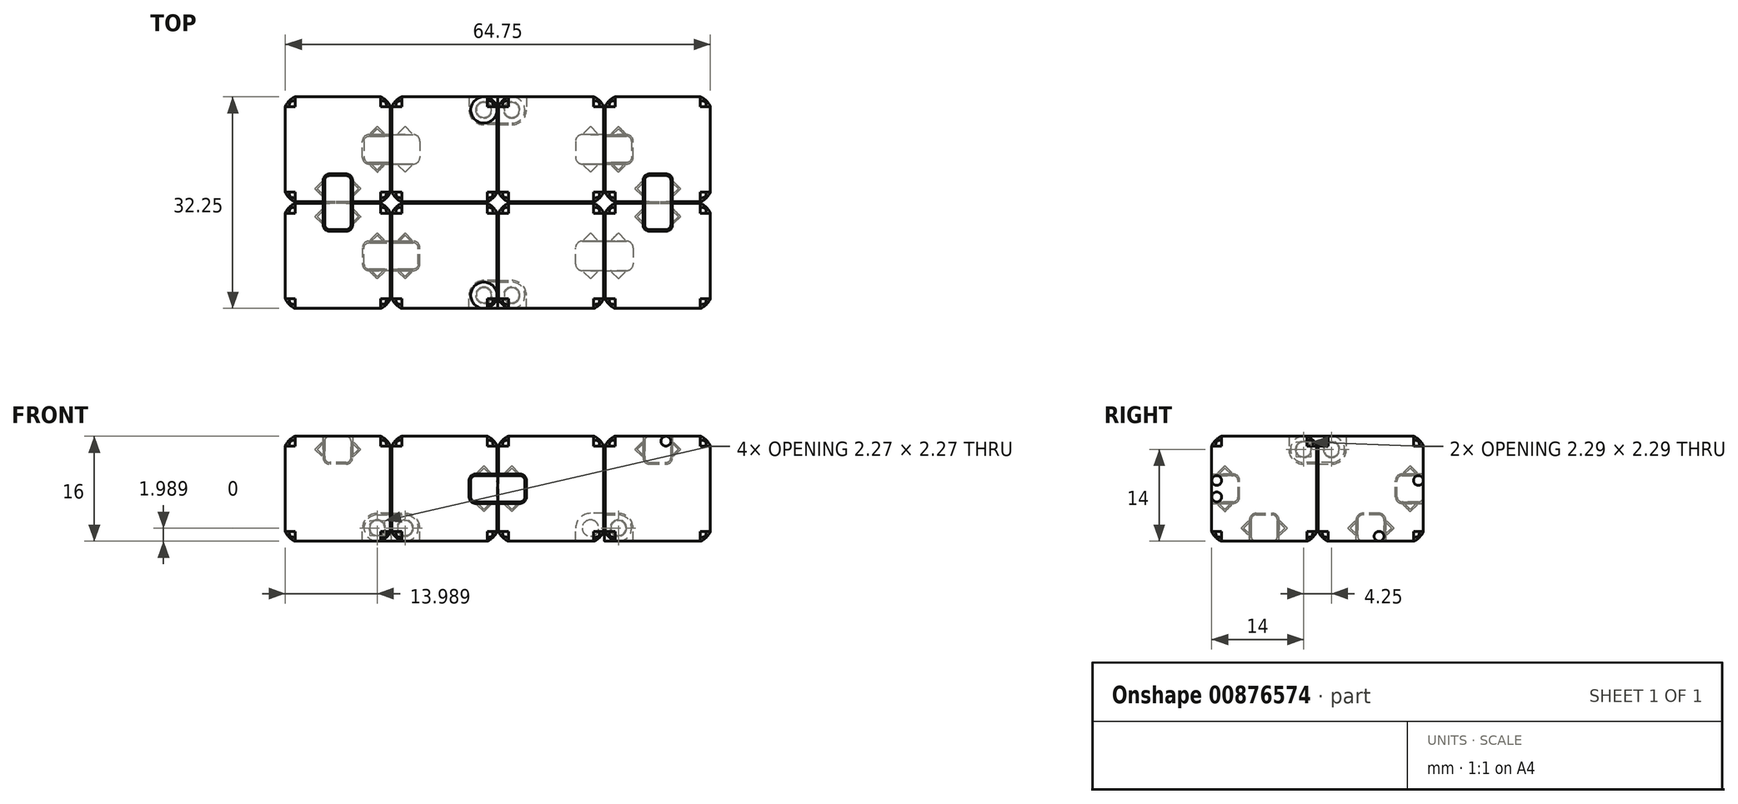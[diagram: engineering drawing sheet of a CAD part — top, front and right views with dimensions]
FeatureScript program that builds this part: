
annotation { "Feature Type Name" : "Feature", "Feature Type Description" : "" }
export const myFeature = defineFeature(function(context is Context, id is Id, definition is map)
    precondition{}
    {
        {
            assignVariable(context, id + "F0", {"name" : "cubeSize", "anyValue" : 16});
        }
        {
            assignVariable(context, id + "F1", {"name" : "hingeSize", "anyValue" : getVariable(context, 'cubeSize') / 4});
        }
        {
            assignVariable(context, id + "F2", {"name" : "hingeDiameter", "anyValue" : getVariable(context, 'hingeSize') / 2});
        }
        {
            assignVariable(context, id + "F3", {"name" : "minThickness", "anyValue" : 1});
        }
        {
            assignVariable(context, id + "F4", {"name" : "hingeGap", "anyValue" : .25});
        }
        {
            var Q0;
            Q0=qCreatedBy(makeId("Top.planeOp"),FACE);
            var sketch = newSketch(context, id + "F5", { "sketchPlane" : qUnion([Q0])});
            skLineSegment(sketch, "E0.bottom", {"start": v(8, -8) * mm, "end": v(-8, -8) * mm});
            skLineSegment(sketch, "E0.top", {"start": v(8, 8) * mm, "end": v(-8, 8) * mm});
            skLineSegment(sketch, "E0.left", {"start": v(8, -8) * mm, "end": v(8, 8) * mm});
            skLineSegment(sketch, "E0.right", {"start": v(-8, -8) * mm, "end": v(-8, 8) * mm});
            skPoint(sketch, "E0.middle", {"position": v(0, 0) * mm});
            skSolve(sketch);
        }
        {
            var Q0;
            Q0=qSketchRegion(id+"F5",true);
            extrude(context, id + "F6", {"entities" : qUnion([Q0]), "depth" : (getVariable(context, 'cubeSize')) * mm, "offsetDistance" : 25 * mm});
        }
        {
            var Q0;
            Q0=qCreatedBy(makeId("Front.planeOp"),FACE);
            var sketch = newSketch(context, id + "F7", { "sketchPlane" : qUnion([Q0])});
            skCircle(sketch, "E1", {"center": v(6, 2) * mm, "radius": 1 * mm});
            skLineSegment(sketch, "E2", {"start": v(6, 2) * mm, "end": v(7, 2) * mm, "construction": true});
            skLineSegment(sketch, "E3", {"start": v(7, 2) * mm, "end": v(8, 2) * mm, "construction": true});
            skLineSegment(sketch, "E4", {"start": v(6, 0) * mm, "end": v(6, 1) * mm, "construction": true});
            skLineSegment(sketch, "E5", {"start": v(6, 1) * mm, "end": v(6, 2) * mm, "construction": true});
            skLineSegment(sketch, "E6", {"start": v(8, 0) * mm, "end": v(3.75, 0) * mm});
            skLineSegment(sketch, "E7", {"start": v(3.75, 0) * mm, "end": v(3.75, 2) * mm});
            skLineSegment(sketch, "E8", {"start": v(8, 0) * mm, "end": v(8, 4.25) * mm});
            skLineSegment(sketch, "E9", {"start": v(8, 4.25) * mm, "end": v(6, 4.25) * mm});
            skArc(sketch, "E10", {"start": v(6, 4.25) * mm, "mid": v(4.4, 3.6) * mm, "end": v(3.75, 2) * mm});
            skSolve(sketch);
        }
        {
            var Q0;
            Q0=makeQuery(id+"F7.imprint","IMPRINT",FACE,{"disambiguationData":[TD([[makeQuery(id+"F7.imprint","IMPRINT",EDGE,{"derivedFrom":sQuery(id+"F7.wireOp",EDGE,"E1")}),-1.0]])]});
            var Q1;
            Q1=makeQuery(id+"F7.imprint","IMPRINT",FACE,{"disambiguationData":[TD([[makeQuery(id+"F7.imprint","IMPRINT",EDGE,{"derivedFrom":sQuery(id+"F7.wireOp",EDGE,"E1")}),1.0]])]});
            extrude(context, id + "F8", {"entities" : qUnion([Q0, Q1]), "operationType" : NewBodyOperationType.REMOVE, "endBound" : BoundingType.SYMMETRIC, "oppositeDirection" : true, "depth" : (getVariable(context, 'hingeSize') + getVariable(context, 'hingeGap') * 2) * mm, "offsetDistance" : 25 * mm});
        }
        {
            var Q0;
            Q0=makeQuery(id+"F6.opExtrude","CAP_VERTEX",VERTEX,{"disambiguationData":[OSD([sQuery(id+"F5.wireOp",EDGE,"E0.bottom"),sQuery(id+"F5.wireOp",EDGE,"E0.right")])],"isStart":false});
            var Q1;
            Q1=makeQuery(id+"F6.opExtrude","CAP_VERTEX",VERTEX,{"disambiguationData":[OSD([sQuery(id+"F5.wireOp",EDGE,"E0.bottom"),sQuery(id+"F5.wireOp",EDGE,"E0.left")])],"isStart":true});
            var Q2;
            Q2=makeQuery(id+"F6.opExtrude","CAP_VERTEX",VERTEX,{"disambiguationData":[OSD([sQuery(id+"F5.wireOp",EDGE,"E0.top"),sQuery(id+"F5.wireOp",EDGE,"E0.left")])],"isStart":true});
            cPlane(context, id + "F9", {"entities" : qUnion([Q0, Q1, Q2]), "cplaneType" : CPlaneType.THREE_POINT, "offset" : 25 * mm, "width" : 150 * mm, "height" : 150 * mm});
        }
        {
            var Q0;
            Q0=qCreatedBy(id+"F9.planeOp",FACE);
            var sketch = newSketch(context, id + "F10", { "sketchPlane" : qUnion([Q0])});
            skLineSegment(sketch, "E11", {"start": v(2.25, -1.58) * mm, "end": v(-2.25, -1.58) * mm});
            skLineSegment(sketch, "E12", {"start": v(-2.25, -1.58) * mm, "end": v(-3.5, -2.83) * mm});
            skLineSegment(sketch, "E13", {"start": v(-3.5, -2.83) * mm, "end": v(3.5, -2.83) * mm});
            skLineSegment(sketch, "E14", {"start": v(3.5, -2.83) * mm, "end": v(2.25, -1.58) * mm});
            skSolve(sketch);
        }
        {
            var Q0;
            Q0=makeQuery(id+"F10.imprint","IMPRINT",FACE,{"disambiguationData":[TD([[makeQuery(id+"F10.imprint","IMPRINT",EDGE,{"derivedFrom":sQuery(id+"F10.wireOp",EDGE,"E11")}),1.0]])]});
            var Q1;
            Q1=sQuery(id+"F10.wireOp",EDGE,"E13");
            revolve(context, id + "F11", {"operationType" : NewBodyOperationType.REMOVE, "entities" : qUnion([Q0]), "axis" : qUnion([Q1]), "revolveType" : RevolveType.FULL, "oppositeDirection" : true});
        }
        {
            var Q0;
            Q0=qCreatedBy(makeId("Right.planeOp"),FACE);
            var sketch = newSketch(context, id + "F12", { "sketchPlane" : qUnion([Q0])});
            skCircle(sketch, "E15", {"center": v(6, 14) * mm, "radius": 1 * mm});
            skLineSegment(sketch, "E16", {"start": v(3.75, 16) * mm, "end": v(8, 16) * mm});
            skLineSegment(sketch, "E17", {"start": v(8, 16) * mm, "end": v(8, 11.75) * mm});
            skLineSegment(sketch, "E18", {"start": v(8, 11.75) * mm, "end": v(6, 11.75) * mm});
            skLineSegment(sketch, "E19", {"start": v(3.75, 16) * mm, "end": v(3.75, 14) * mm});
            skLineSegment(sketch, "E20", {"start": v(6, 14) * mm, "end": v(7, 14) * mm, "construction": true});
            skLineSegment(sketch, "E21", {"start": v(7, 14) * mm, "end": v(8, 14) * mm, "construction": true});
            skLineSegment(sketch, "E22", {"start": v(6, 14) * mm, "end": v(6, 15) * mm, "construction": true});
            skLineSegment(sketch, "E23", {"start": v(6, 15) * mm, "end": v(6, 16) * mm, "construction": true});
            skArc(sketch, "E24", {"start": v(3.75, 14) * mm, "mid": v(4.4, 12.4) * mm, "end": v(6, 11.75) * mm});
            skSolve(sketch);
        }
        {
            var Q0;
            Q0=makeQuery(id+"F12.imprint","IMPRINT",FACE,{"disambiguationData":[TD([[makeQuery(id+"F12.imprint","IMPRINT",EDGE,{"derivedFrom":sQuery(id+"F12.wireOp",EDGE,"E15")}),1.0]])]});
            var Q1;
            Q1=makeQuery(id+"F12.imprint","IMPRINT",FACE,{"disambiguationData":[TD([[makeQuery(id+"F12.imprint","IMPRINT",EDGE,{"derivedFrom":sQuery(id+"F12.wireOp",EDGE,"E15")}),-1.0]])]});
            extrude(context, id + "F13", {"entities" : qUnion([Q0, Q1]), "operationType" : NewBodyOperationType.REMOVE, "endBound" : BoundingType.SYMMETRIC, "depth" : (getVariable(context, 'hingeSize') + getVariable(context, 'hingeGap') * 2) * mm, "offsetDistance" : 25 * mm});
        }
        {
            var Q0;
            Q0=makeQuery(id+"F6.opExtrude","CAP_VERTEX",VERTEX,{"disambiguationData":[OSD([sQuery(id+"F5.wireOp",EDGE,"E0.top"),sQuery(id+"F5.wireOp",EDGE,"E0.left")])],"isStart":false});
            var Q1;
            Q1=makeQuery(id+"F6.opExtrude","CAP_VERTEX",VERTEX,{"disambiguationData":[OSD([sQuery(id+"F5.wireOp",EDGE,"E0.top"),sQuery(id+"F5.wireOp",EDGE,"E0.right")])],"isStart":false});
            var Q2;
            Q2=makeQuery(id+"F6.opExtrude","CAP_VERTEX",VERTEX,{"disambiguationData":[OSD([sQuery(id+"F5.wireOp",EDGE,"E0.bottom"),sQuery(id+"F5.wireOp",EDGE,"E0.right")])],"isStart":true});
            cPlane(context, id + "F14", {"entities" : qUnion([Q0, Q1, Q2]), "cplaneType" : CPlaneType.THREE_POINT, "offset" : 25 * mm, "width" : 150 * mm, "height" : 150 * mm});
        }
        {
            var Q0;
            Q0=qCreatedBy(id+"F14.planeOp",FACE);
            var sketch = newSketch(context, id + "F15", { "sketchPlane" : qUnion([Q0])});
            skLineSegment(sketch, "E25", {"start": v(-3.5, 14.14) * mm, "end": v(3.5, 14.14) * mm});
            skLineSegment(sketch, "E26", {"start": v(3.5, 14.14) * mm, "end": v(2.25, 12.9) * mm});
            skLineSegment(sketch, "E27", {"start": v(2.25, 12.9) * mm, "end": v(-2.25, 12.9) * mm});
            skLineSegment(sketch, "E28", {"start": v(-2.25, 12.9) * mm, "end": v(-3.5, 14.14) * mm});
            skSolve(sketch);
        }
        {
            var Q0;
            Q0=qSketchRegion(id+"F15",true);
            var Q1;
            Q1=sQuery(id+"F15.wireOp",EDGE,"E25");
            revolve(context, id + "F16", {"operationType" : NewBodyOperationType.REMOVE, "entities" : qUnion([Q0]), "axis" : qUnion([Q1]), "revolveType" : RevolveType.FULL, "oppositeDirection" : true});
        }
        {
            var Q0;
            Q0=makeQuery(id+"F6.opExtrude","SWEPT_FACE",FACE,{"disambiguationData":[OSD([sQuery(id+"F5.wireOp",EDGE,"E0.right")])]});
            var Q1;
            Q1=makeQuery(id+"F6.opExtrude","SWEPT_FACE",FACE,{"disambiguationData":[OSD([sQuery(id+"F5.wireOp",EDGE,"E0.bottom")])]});
            var Q2;
            {var subQ0=sQuery(id+"F5.wireOp",EDGE,"E0.right");var subQ1=sQuery(id+"F5.wireOp",EDGE,"E0.top");Q2=makeQuery(id+"F13.boolean.opBoolean","SPLIT",EDGE,{"disambiguationData":[TD([makeQuery(id+"F6.opExtrude","SWEPT_FACE",FACE,{"disambiguationData":[OSD([subQ0])]})])],"derivedFrom":makeQuery(id+"F6.opExtrude","CAP_EDGE",EDGE,{"disambiguationData":[OSD([subQ1])],"isStart":false})});}
            var Q3;
            {var subQ0=sQuery(id+"F5.wireOp",EDGE,"E0.left");var subQ1=sQuery(id+"F5.wireOp",EDGE,"E0.top");Q3=makeQuery(id+"F13.boolean.opBoolean","SPLIT",EDGE,{"disambiguationData":[TD([makeQuery(id+"F6.opExtrude","SWEPT_FACE",FACE,{"disambiguationData":[OSD([subQ0])]})])],"derivedFrom":makeQuery(id+"F6.opExtrude","CAP_EDGE",EDGE,{"disambiguationData":[OSD([subQ1])],"isStart":false})});}
            var Q4;
            Q4=makeQuery(id+"F6.opExtrude","CAP_EDGE",EDGE,{"disambiguationData":[OSD([sQuery(id+"F5.wireOp",EDGE,"E0.left")])],"isStart":false});
            var Q5;
            Q5=makeQuery(id+"F6.opExtrude","SWEPT_EDGE",EDGE,{"disambiguationData":[OSD([sQuery(id+"F5.wireOp",EDGE,"E0.top"),sQuery(id+"F5.wireOp",EDGE,"E0.left")])]});
            var Q6;
            {var subQ0=sQuery(id+"F5.wireOp",EDGE,"E0.left");var subQ1=sQuery(id+"F5.wireOp",EDGE,"E0.top");Q6=makeQuery(id+"F8.boolean.opBoolean","SPLIT",EDGE,{"disambiguationData":[TD([makeQuery(id+"F6.opExtrude","SWEPT_FACE",FACE,{"disambiguationData":[OSD([subQ1])]})])],"derivedFrom":makeQuery(id+"F6.opExtrude","CAP_EDGE",EDGE,{"disambiguationData":[OSD([subQ0])],"isStart":true})});}
            var Q7;
            Q7=makeQuery(id+"F6.opExtrude","CAP_EDGE",EDGE,{"disambiguationData":[OSD([sQuery(id+"F5.wireOp",EDGE,"E0.top")])],"isStart":true});
            var Q8;
            {var subQ0=sQuery(id+"F5.wireOp",EDGE,"E0.bottom");var subQ1=sQuery(id+"F5.wireOp",EDGE,"E0.left");Q8=makeQuery(id+"F8.boolean.opBoolean","SPLIT",EDGE,{"disambiguationData":[TD([makeQuery(id+"F6.opExtrude","SWEPT_FACE",FACE,{"disambiguationData":[OSD([subQ0])]})])],"derivedFrom":makeQuery(id+"F6.opExtrude","CAP_EDGE",EDGE,{"disambiguationData":[OSD([subQ1])],"isStart":true})});}
            fillet(context, id + "F17", {"entities" : qUnion([Q0, Q1, Q2, Q3, Q4, Q5, Q6, Q7, Q8]), "radius" : (getVariable(context, 'hingeDiameter') / 2 + getVariable(context, 'minThickness') - .5) * mm, "tangentPropagation" : true, "rho" : .2, "crossSection" : FilletCrossSection.CONIC, "allowEdgeOverflow" : false});
        }
        {
            var Q0;
            Q0=makeQuery(id+"F8.boolean.opBoolean","COPY",EDGE,{"derivedFrom":makeQuery(id+"F8.opExtrude","CAP_EDGE",EDGE,{"disambiguationData":[OSD([sQuery(id+"F7.wireOp",EDGE,"E7")])],"isStart":true})});
            var Q1;
            Q1=makeQuery(id+"F8.boolean.opBoolean","COPY",EDGE,{"derivedFrom":makeQuery(id+"F8.opExtrude","CAP_EDGE",EDGE,{"disambiguationData":[OSD([sQuery(id+"F7.wireOp",EDGE,"E7")])],"isStart":false})});
            var Q2;
            Q2=makeQuery(id+"F13.boolean.opBoolean","COPY",EDGE,{"derivedFrom":makeQuery(id+"F13.opExtrude","CAP_EDGE",EDGE,{"disambiguationData":[OSD([sQuery(id+"F12.wireOp",EDGE,"E18")])],"isStart":false})});
            var Q3;
            Q3=makeQuery(id+"F13.boolean.opBoolean","COPY",EDGE,{"derivedFrom":makeQuery(id+"F13.opExtrude","CAP_EDGE",EDGE,{"disambiguationData":[OSD([sQuery(id+"F12.wireOp",EDGE,"E18")])],"isStart":true})});
            fillet(context, id + "F18", {"entities" : qUnion([Q0, Q1, Q2, Q3]), "radius" : (getVariable(context, 'minThickness')) * mm, "tangentPropagation" : true, "allowEdgeOverflow" : false});
        }
        {
            var Q0;
            Q0=qCreatedBy(makeId("Front.planeOp"),FACE);
            var sketch = newSketch(context, id + "F19", { "sketchPlane" : qUnion([Q0])});
            skCircle(sketch, "E29", {"center": v(6, 2) * mm, "radius": 1 * mm, "construction": true});
            skArc(sketch, "E30", {"start": v(6, 4) * mm, "mid": v(4, 2) * mm, "end": v(6, 0) * mm});
            skArc(sketch, "E31", {"start": v(10.25, 0) * mm, "mid": v(12.25, 2) * mm, "end": v(10.25, 4) * mm});
            skLineSegment(sketch, "E32", {"start": v(6, 2) * mm, "end": v(8, 2) * mm, "construction": true});
            skCircle(sketch, "E33", {"center": v(10.25, 2) * mm, "radius": 1 * mm, "construction": true});
            skLineSegment(sketch, "E34", {"start": v(8, 2) * mm, "end": v(8.25, 2) * mm, "construction": true});
            skLineSegment(sketch, "E35", {"start": v(8.25, 2) * mm, "end": v(10.25, 2) * mm, "construction": true});
            skLineSegment(sketch, "E36", {"start": v(8.12, 0) * mm, "end": v(8.12, 2) * mm});
            skLineSegment(sketch, "E37", {"start": v(8.12, 2) * mm, "end": v(8.12, 4) * mm});
            skLineSegment(sketch, "E38", {"start": v(10.25, 0) * mm, "end": v(6, 0) * mm});
            skLineSegment(sketch, "E39", {"start": v(10.25, 4) * mm, "end": v(6, 4) * mm});
            skSolve(sketch);
        }
        {
            var Q0;
            Q0=makeQuery(id+"F19.imprint","IMPRINT",FACE,{"disambiguationData":[TD([[makeQuery(id+"F19.imprint","IMPRINT",EDGE,{"derivedFrom":sQuery(id+"F19.wireOp",EDGE,"E30")}),1.0]])]});
            extrude(context, id + "F20", {"entities" : qUnion([Q0]), "endBound" : BoundingType.SYMMETRIC, "depth" : (getVariable(context, 'hingeSize')) * mm, "offsetDistance" : 25 * mm});
        }
        {
            var Q0;
            Q0=qCreatedBy(id+"F9.planeOp",FACE);
            var sketch = newSketch(context, id + "F21", { "sketchPlane" : qUnion([Q0])});
            skLineSegment(sketch, "E40", {"start": v(3.15, -2.83) * mm, "end": v(1.9, -1.58) * mm});
            skLineSegment(sketch, "E41", {"start": v(1.9, -1.58) * mm, "end": v(-1.9, -1.58) * mm});
            skLineSegment(sketch, "E42", {"start": v(-1.9, -1.58) * mm, "end": v(-3.15, -2.83) * mm});
            skLineSegment(sketch, "E43", {"start": v(-3.15, -2.83) * mm, "end": v(3.15, -2.83) * mm});
            skSolve(sketch);
        }
        {
            var Q0;
            Q0=qSketchRegion(id+"F21",true);
            var Q1;
            Q1=sQuery(id+"F21.wireOp",EDGE,"E43");
            revolve(context, id + "F22", {"operationType" : NewBodyOperationType.ADD, "entities" : qUnion([Q0]), "axis" : qUnion([Q1]), "revolveType" : RevolveType.FULL});
        }
        {
            var Q0;
            Q0=qCreatedBy(makeId("Right.planeOp"),FACE);
            var sketch = newSketch(context, id + "F23", { "sketchPlane" : qUnion([Q0])});
            skCircle(sketch, "E44", {"center": v(6, 14) * mm, "radius": 1.25 * mm, "construction": true});
            skArc(sketch, "E45", {"start": v(6, 16) * mm, "mid": v(4, 14) * mm, "end": v(6, 12) * mm});
            skArc(sketch, "E46", {"start": v(10.25, 12) * mm, "mid": v(12.25, 14) * mm, "end": v(10.25, 16) * mm});
            skLineSegment(sketch, "E47", {"start": v(6, 14) * mm, "end": v(8, 14) * mm, "construction": true});
            skCircle(sketch, "E48", {"center": v(10.25, 14) * mm, "radius": 1 * mm, "construction": true});
            skLineSegment(sketch, "E49", {"start": v(8, 14) * mm, "end": v(8.25, 14) * mm, "construction": true});
            skLineSegment(sketch, "E50", {"start": v(8.25, 14) * mm, "end": v(10.25, 14) * mm, "construction": true});
            skLineSegment(sketch, "E51", {"start": v(8.12, 12) * mm, "end": v(8.12, 14) * mm});
            skLineSegment(sketch, "E52", {"start": v(8.12, 14) * mm, "end": v(8.12, 16) * mm});
            skLineSegment(sketch, "E53", {"start": v(10.25, 12) * mm, "end": v(6, 12) * mm});
            skLineSegment(sketch, "E54", {"start": v(10.25, 16) * mm, "end": v(6, 16) * mm});
            skSolve(sketch);
        }
        {
            var Q0;
            {var subQ3=sQuery(id+"F23.wireOp",EDGE,"E45");Q0=makeQuery(id+"F23.imprint","IMPRINT",FACE,{"disambiguationData":[TD([[makeQuery(id+"F23.imprint","IMPRINT",EDGE,{"derivedFrom":subQ3}),1.0]])]});}
            extrude(context, id + "F24", {"entities" : qUnion([Q0]), "endBound" : BoundingType.SYMMETRIC, "depth" : (getVariable(context, 'hingeSize')) * mm, "offsetDistance" : 25 * mm});
        }
        {
            var Q0;
            Q0=makeQuery(id+"F20.opExtrude","CAP_EDGE",EDGE,{"disambiguationData":[OSD([sQuery(id+"F19.wireOp",EDGE,"E38")])],"isStart":false});
            var Q1;
            Q1=makeQuery(id+"F20.opExtrude","CAP_EDGE",EDGE,{"disambiguationData":[OSD([sQuery(id+"F19.wireOp",EDGE,"E38")])],"isStart":true});
            var Q2;
            Q2=makeQuery(id+"F24.opExtrude","CAP_EDGE",EDGE,{"disambiguationData":[OSD([sQuery(id+"F23.wireOp",EDGE,"E54")])],"isStart":false});
            var Q3;
            Q3=makeQuery(id+"F24.opExtrude","CAP_EDGE",EDGE,{"disambiguationData":[OSD([sQuery(id+"F23.wireOp",EDGE,"E54")])],"isStart":true});
            fillet(context, id + "F25", {"entities" : qUnion([Q0, Q1, Q2, Q3]), "radius" : (getVariable(context, 'minThickness') - getVariable(context, 'hingeGap')) * mm, "tangentPropagation" : true, "allowEdgeOverflow" : false});
        }
        {
            var Q0;
            Q0=qCreatedBy(id+"F14.planeOp",FACE);
            var sketch = newSketch(context, id + "F26", { "sketchPlane" : qUnion([Q0])});
            skLineSegment(sketch, "E55", {"start": v(-3.15, 14.14) * mm, "end": v(3.15, 14.14) * mm});
            skLineSegment(sketch, "E56", {"start": v(3.15, 14.14) * mm, "end": v(1.9, 12.9) * mm});
            skLineSegment(sketch, "E57", {"start": v(1.9, 12.9) * mm, "end": v(-1.9, 12.9) * mm});
            skLineSegment(sketch, "E58", {"start": v(-1.9, 12.9) * mm, "end": v(-3.15, 14.14) * mm});
            skSolve(sketch);
        }
        {
            var Q0;
            Q0=makeQuery(id+"F26.imprint","IMPRINT",FACE,{"disambiguationData":[TD([[makeQuery(id+"F26.imprint","IMPRINT",EDGE,{"derivedFrom":sQuery(id+"F26.wireOp",EDGE,"E55")}),-1.0]])]});
            var Q1;
            Q1=sQuery(id+"F26.wireOp",EDGE,"E55");
            revolve(context, id + "F27", {"operationType" : NewBodyOperationType.ADD, "entities" : qUnion([Q0]), "axis" : qUnion([Q1]), "revolveType" : RevolveType.FULL});
        }
        {
            var Q0;
            Q0=makeQuery(id+"F20.opExtrude","SWEPT_FACE",FACE,{"disambiguationData":[OSD([sQuery(id+"F19.wireOp",EDGE,"E36"),sQuery(id+"F19.wireOp",EDGE,"E37")])]});
            var sketch = newSketch(context, id + "F28", { "sketchPlane" : qUnion([Q0])});
            skLineSegment(sketch, "E59", {"start": v(-7.63, -0.12) * mm, "end": v(6.67, -0.12) * mm, "construction": true});
            skSolve(sketch);
        }
        {
            var Q0;
            Q0=makeQuery(id+"F6.opExtrude","SWEPT_BODY",BODY,{"disambiguationData":[OSD([sQuery(id+"F5.wireOp",EDGE,"E0.bottom"),sQuery(id+"F5.wireOp",EDGE,"E0.top"),sQuery(id+"F5.wireOp",EDGE,"E0.left"),sQuery(id+"F5.wireOp",EDGE,"E0.right")])]});
            var Q1;
            Q1=makeQuery(id+"F24.opExtrude","SWEPT_BODY",BODY,{"disambiguationData":[OSD([sQuery(id+"F23.wireOp",EDGE,"E45"),sQuery(id+"F23.wireOp",EDGE,"E51"),sQuery(id+"F23.wireOp",EDGE,"E52"),sQuery(id+"F23.wireOp",EDGE,"E53"),sQuery(id+"F23.wireOp",EDGE,"E54")])]});
            var Q2;
            Q2=sQuery(id+"F28.wireOp",EDGE,"E59");
            circularPattern(context, id + "F29", {"entities" : qUnion([Q0, Q1]), "axis" : qUnion([Q2]), "angle" : 90 * degree, "instanceCount" : 2});
        }
        {
            var Q0;
            Q0=makeQuery(id+"F29.opPattern","COPY",BODY,{"derivedFrom":makeQuery(id+"F6.opExtrude","SWEPT_BODY",BODY,{"disambiguationData":[OSD([sQuery(id+"F5.wireOp",EDGE,"E0.bottom"),sQuery(id+"F5.wireOp",EDGE,"E0.top"),sQuery(id+"F5.wireOp",EDGE,"E0.left"),sQuery(id+"F5.wireOp",EDGE,"E0.right")])]}),"instanceName":"1"});
            var Q1;
            Q1=makeQuery(id+"F29.opPattern","COPY",BODY,{"derivedFrom":makeQuery(id+"F24.opExtrude","SWEPT_BODY",BODY,{"disambiguationData":[OSD([sQuery(id+"F23.wireOp",EDGE,"E45"),sQuery(id+"F23.wireOp",EDGE,"E51"),sQuery(id+"F23.wireOp",EDGE,"E52"),sQuery(id+"F23.wireOp",EDGE,"E53"),sQuery(id+"F23.wireOp",EDGE,"E54")])]}),"instanceName":"1"});
            var Q2;
            Q2=qCreatedBy(makeId("Front.planeOp"),FACE);
            mirror(context, id + "F30", {"entities" : qUnion([Q0, Q1]), "mirrorPlane" : qUnion([Q2])});
        }
        {
            var Q0;
            Q0=makeQuery(id+"F29.opPattern","COPY",BODY,{"derivedFrom":makeQuery(id+"F24.opExtrude","SWEPT_BODY",BODY,{"disambiguationData":[OSD([sQuery(id+"F23.wireOp",EDGE,"E45"),sQuery(id+"F23.wireOp",EDGE,"E51"),sQuery(id+"F23.wireOp",EDGE,"E52"),sQuery(id+"F23.wireOp",EDGE,"E53"),sQuery(id+"F23.wireOp",EDGE,"E54")])]}),"instanceName":"1"});
            var Q1;
            Q1=makeQuery(id+"F29.opPattern","COPY",BODY,{"derivedFrom":makeQuery(id+"F6.opExtrude","SWEPT_BODY",BODY,{"disambiguationData":[OSD([sQuery(id+"F5.wireOp",EDGE,"E0.bottom"),sQuery(id+"F5.wireOp",EDGE,"E0.top"),sQuery(id+"F5.wireOp",EDGE,"E0.left"),sQuery(id+"F5.wireOp",EDGE,"E0.right")])]}),"instanceName":"1"});
            deleteBodies(context, id + "F31", {"entities" : qUnion([Q0, Q1])});
        }
        {
            var Q0;
            Q0=makeQuery(id+"F20.opExtrude","SWEPT_BODY",BODY,{"disambiguationData":[OSD([sQuery(id+"F19.wireOp",EDGE,"E30"),sQuery(id+"F19.wireOp",EDGE,"E36"),sQuery(id+"F19.wireOp",EDGE,"E37"),sQuery(id+"F19.wireOp",EDGE,"E38"),sQuery(id+"F19.wireOp",EDGE,"E39")])]});
            var Q1;
            Q1=makeQuery(id+"F20.opExtrude","SWEPT_FACE",FACE,{"disambiguationData":[OSD([sQuery(id+"F19.wireOp",EDGE,"E36"),sQuery(id+"F19.wireOp",EDGE,"E37")])]});
            mirror(context, id + "F32", {"operationType" : NewBodyOperationType.ADD, "entities" : qUnion([Q0]), "mirrorPlane" : qUnion([Q1])});
        }
        {
            var Q0;
            {var subQ0=sQuery(id+"F5.wireOp",EDGE,"E0.left");var subQ1=makeQuery(id+"F6.opExtrude","SWEPT_FACE",FACE,{"disambiguationData":[OSD([subQ0])]});var subQ2=sQuery(id+"F5.wireOp",EDGE,"E0.bottom");Q0=makeQuery(id+"F30.opPattern","COPY",VERTEX,{"derivedFrom":makeQuery(id+"F29.opPattern","COPY",VERTEX,{"derivedFrom":makeQuery(id+"F17.opFillet","BLEND_VERTEX",VERTEX,{"blendedFrom":[makeQuery(id+"F6.opExtrude","CAP_VERTEX",VERTEX,{"disambiguationData":[OSD([subQ2,subQ0])],"isStart":true}),makeQuery(id+"F6.opExtrude","SWEPT_EDGE",EDGE,{"disambiguationData":[OSD([subQ2,subQ0])]}),makeQuery(id+"F8.boolean.opBoolean","SPLIT",EDGE,{"disambiguationData":[TD([makeQuery(id+"F6.opExtrude","SWEPT_FACE",FACE,{"disambiguationData":[OSD([subQ2])]})])],"derivedFrom":makeQuery(id+"F6.opExtrude","CAP_EDGE",EDGE,{"disambiguationData":[OSD([subQ0])],"isStart":true})}),subQ1],"blendedInto":[subQ1]}),"instanceName":"1"}),"instanceName":"1"});}
            var Q1;
            {var subQ0=sQuery(id+"F5.wireOp",EDGE,"E0.left");var subQ1=sQuery(id+"F5.wireOp",EDGE,"E0.top");Q1=makeQuery(id+"F30.opPattern","COPY",VERTEX,{"derivedFrom":makeQuery(id+"F29.opPattern","COPY",VERTEX,{"derivedFrom":makeQuery(id+"F17.opFillet","BLEND_VERTEX",VERTEX,{"blendedFrom":[makeQuery(id+"F6.opExtrude","CAP_VERTEX",VERTEX,{"disambiguationData":[OSD([subQ1,subQ0])],"isStart":false}),makeQuery(id+"F6.opExtrude","SWEPT_EDGE",EDGE,{"disambiguationData":[OSD([subQ1,subQ0])]}),makeQuery(id+"F6.opExtrude","CAP_EDGE",EDGE,{"disambiguationData":[OSD([subQ0])],"isStart":false}),makeQuery(id+"F6.opExtrude","SWEPT_FACE",FACE,{"disambiguationData":[OSD([subQ0])]})],"blendedInto":[makeQuery(id+"F6.opExtrude","SWEPT_FACE",FACE,{"disambiguationData":[OSD([subQ0])]})]}),"instanceName":"1"}),"instanceName":"1"});}
            var Q2;
            {var subQ0=sQuery(id+"F5.wireOp",EDGE,"E0.right");var subQ1=sQuery(id+"F5.wireOp",EDGE,"E0.top");Q2=makeQuery(id+"F30.opPattern","COPY",VERTEX,{"derivedFrom":makeQuery(id+"F29.opPattern","COPY",VERTEX,{"derivedFrom":makeQuery(id+"F17.opFillet","BLEND_VERTEX",VERTEX,{"blendedFrom":[makeQuery(id+"F6.opExtrude","CAP_VERTEX",VERTEX,{"disambiguationData":[OSD([subQ1,subQ0])],"isStart":false}),makeQuery(id+"F6.opExtrude","SWEPT_EDGE",EDGE,{"disambiguationData":[OSD([subQ1,subQ0])]}),makeQuery(id+"F6.opExtrude","CAP_EDGE",EDGE,{"disambiguationData":[OSD([subQ0])],"isStart":false}),makeQuery(id+"F6.opExtrude","SWEPT_FACE",FACE,{"disambiguationData":[OSD([subQ0])]})],"blendedInto":[makeQuery(id+"F6.opExtrude","SWEPT_FACE",FACE,{"disambiguationData":[OSD([subQ0])]})]}),"instanceName":"1"}),"instanceName":"1"});}
            cPlane(context, id + "F33", {"entities" : qUnion([Q0, Q1, Q2]), "cplaneType" : CPlaneType.THREE_POINT, "offset" : 25 * mm, "width" : 150 * mm, "height" : 150 * mm});
        }
        {
            var Q0;
            Q0=qCreatedBy(id+"F33.planeOp",FACE);
            var sketch = newSketch(context, id + "F34", { "sketchPlane" : qUnion([Q0])});
            skLineSegment(sketch, "E60", {"start": v(-19.98, 11.15) * mm, "end": v(-19.98, 4.85) * mm, "construction": true});
            skSolve(sketch);
        }
        {
            var Q0;
            Q0=makeQuery(id+"F30.opPattern","COPY",BODY,{"derivedFrom":makeQuery(id+"F29.opPattern","COPY",BODY,{"derivedFrom":makeQuery(id+"F24.opExtrude","SWEPT_BODY",BODY,{"disambiguationData":[OSD([sQuery(id+"F23.wireOp",EDGE,"E45"),sQuery(id+"F23.wireOp",EDGE,"E51"),sQuery(id+"F23.wireOp",EDGE,"E52"),sQuery(id+"F23.wireOp",EDGE,"E53"),sQuery(id+"F23.wireOp",EDGE,"E54")])]}),"instanceName":"1"}),"instanceName":"1"});
            var Q1;
            Q1=sQuery(id+"F34.wireOp",EDGE,"E60");
            circularPattern(context, id + "F35", {"entities" : qUnion([Q0]), "axis" : qUnion([Q1]), "angle" : 90 * degree, "instanceCount" : 2, "oppositeDirection" : true});
        }
        {
            var Q0;
            Q0=makeQuery(id+"F30.opPattern","COPY",BODY,{"derivedFrom":makeQuery(id+"F29.opPattern","COPY",BODY,{"derivedFrom":makeQuery(id+"F24.opExtrude","SWEPT_BODY",BODY,{"disambiguationData":[OSD([sQuery(id+"F23.wireOp",EDGE,"E45"),sQuery(id+"F23.wireOp",EDGE,"E51"),sQuery(id+"F23.wireOp",EDGE,"E52"),sQuery(id+"F23.wireOp",EDGE,"E53"),sQuery(id+"F23.wireOp",EDGE,"E54")])]}),"instanceName":"1"}),"instanceName":"1"});
            deleteBodies(context, id + "F36", {"entities" : qUnion([Q0])});
        }
        {
            var Q0;
            Q0=makeQuery(id+"F24.opExtrude","SWEPT_BODY",BODY,{"disambiguationData":[OSD([sQuery(id+"F23.wireOp",EDGE,"E45"),sQuery(id+"F23.wireOp",EDGE,"E51"),sQuery(id+"F23.wireOp",EDGE,"E52"),sQuery(id+"F23.wireOp",EDGE,"E53"),sQuery(id+"F23.wireOp",EDGE,"E54")])]});
            var Q1;
            Q1=makeQuery(id+"F6.opExtrude","SWEPT_BODY",BODY,{"disambiguationData":[OSD([sQuery(id+"F5.wireOp",EDGE,"E0.bottom"),sQuery(id+"F5.wireOp",EDGE,"E0.top"),sQuery(id+"F5.wireOp",EDGE,"E0.left"),sQuery(id+"F5.wireOp",EDGE,"E0.right")])]});
            var Q2;
            Q2=makeQuery(id+"F20.opExtrude","SWEPT_BODY",BODY,{"disambiguationData":[OSD([sQuery(id+"F19.wireOp",EDGE,"E30"),sQuery(id+"F19.wireOp",EDGE,"E36"),sQuery(id+"F19.wireOp",EDGE,"E37"),sQuery(id+"F19.wireOp",EDGE,"E38"),sQuery(id+"F19.wireOp",EDGE,"E39")])]});
            var Q3;
            Q3=makeQuery(id+"F30.opPattern","COPY",BODY,{"derivedFrom":makeQuery(id+"F29.opPattern","COPY",BODY,{"derivedFrom":makeQuery(id+"F6.opExtrude","SWEPT_BODY",BODY,{"disambiguationData":[OSD([sQuery(id+"F5.wireOp",EDGE,"E0.bottom"),sQuery(id+"F5.wireOp",EDGE,"E0.top"),sQuery(id+"F5.wireOp",EDGE,"E0.left"),sQuery(id+"F5.wireOp",EDGE,"E0.right")])]}),"instanceName":"1"}),"instanceName":"1"});
            var Q4;
            Q4=makeQuery(id+"F35.opPattern","COPY",BODY,{"derivedFrom":makeQuery(id+"F30.opPattern","COPY",BODY,{"derivedFrom":makeQuery(id+"F29.opPattern","COPY",BODY,{"derivedFrom":makeQuery(id+"F24.opExtrude","SWEPT_BODY",BODY,{"disambiguationData":[OSD([sQuery(id+"F23.wireOp",EDGE,"E45"),sQuery(id+"F23.wireOp",EDGE,"E51"),sQuery(id+"F23.wireOp",EDGE,"E52"),sQuery(id+"F23.wireOp",EDGE,"E53"),sQuery(id+"F23.wireOp",EDGE,"E54")])]}),"instanceName":"1"}),"instanceName":"1"}),"instanceName":"1"});
            var Q5;
            Q5=makeQuery(id+"F24.opExtrude","SWEPT_FACE",FACE,{"disambiguationData":[OSD([sQuery(id+"F23.wireOp",EDGE,"E51"),sQuery(id+"F23.wireOp",EDGE,"E52")])]});
            mirror(context, id + "F37", {"operationType" : NewBodyOperationType.ADD, "entities" : qUnion([Q0, Q1, Q2, Q3, Q4]), "mirrorPlane" : qUnion([Q5])});
        }
        {
            var Q0;
            Q0=makeQuery(id+"F35.opPattern","COPY",BODY,{"derivedFrom":makeQuery(id+"F30.opPattern","COPY",BODY,{"derivedFrom":makeQuery(id+"F29.opPattern","COPY",BODY,{"derivedFrom":makeQuery(id+"F24.opExtrude","SWEPT_BODY",BODY,{"disambiguationData":[OSD([sQuery(id+"F23.wireOp",EDGE,"E45"),sQuery(id+"F23.wireOp",EDGE,"E51"),sQuery(id+"F23.wireOp",EDGE,"E52"),sQuery(id+"F23.wireOp",EDGE,"E53"),sQuery(id+"F23.wireOp",EDGE,"E54")])]}),"instanceName":"1"}),"instanceName":"1"}),"instanceName":"1"});
            var Q1;
            Q1=makeQuery(id+"F37.opPattern","COPY",BODY,{"derivedFrom":makeQuery(id+"F35.opPattern","COPY",BODY,{"derivedFrom":makeQuery(id+"F30.opPattern","COPY",BODY,{"derivedFrom":makeQuery(id+"F29.opPattern","COPY",BODY,{"derivedFrom":makeQuery(id+"F24.opExtrude","SWEPT_BODY",BODY,{"disambiguationData":[OSD([sQuery(id+"F23.wireOp",EDGE,"E45"),sQuery(id+"F23.wireOp",EDGE,"E51"),sQuery(id+"F23.wireOp",EDGE,"E52"),sQuery(id+"F23.wireOp",EDGE,"E53"),sQuery(id+"F23.wireOp",EDGE,"E54")])]}),"instanceName":"1"}),"instanceName":"1"}),"instanceName":"1"}),"instanceName":"1"});
            var Q2;
            Q2=makeQuery(id+"F24.opExtrude","SWEPT_BODY",BODY,{"disambiguationData":[OSD([sQuery(id+"F23.wireOp",EDGE,"E45"),sQuery(id+"F23.wireOp",EDGE,"E51"),sQuery(id+"F23.wireOp",EDGE,"E52"),sQuery(id+"F23.wireOp",EDGE,"E53"),sQuery(id+"F23.wireOp",EDGE,"E54")])]});
            var Q3;
            Q3=makeQuery(id+"F37.opPattern","COPY",BODY,{"derivedFrom":makeQuery(id+"F20.opExtrude","SWEPT_BODY",BODY,{"disambiguationData":[OSD([sQuery(id+"F19.wireOp",EDGE,"E30"),sQuery(id+"F19.wireOp",EDGE,"E36"),sQuery(id+"F19.wireOp",EDGE,"E37"),sQuery(id+"F19.wireOp",EDGE,"E38"),sQuery(id+"F19.wireOp",EDGE,"E39")])]}),"instanceName":"1"});
            var Q4;
            Q4=makeQuery(id+"F20.opExtrude","SWEPT_BODY",BODY,{"disambiguationData":[OSD([sQuery(id+"F19.wireOp",EDGE,"E30"),sQuery(id+"F19.wireOp",EDGE,"E36"),sQuery(id+"F19.wireOp",EDGE,"E37"),sQuery(id+"F19.wireOp",EDGE,"E38"),sQuery(id+"F19.wireOp",EDGE,"E39")])]});
            var Q5;
            Q5=makeQuery(id+"F37.opPattern","COPY",BODY,{"derivedFrom":makeQuery(id+"F30.opPattern","COPY",BODY,{"derivedFrom":makeQuery(id+"F29.opPattern","COPY",BODY,{"derivedFrom":makeQuery(id+"F6.opExtrude","SWEPT_BODY",BODY,{"disambiguationData":[OSD([sQuery(id+"F5.wireOp",EDGE,"E0.bottom"),sQuery(id+"F5.wireOp",EDGE,"E0.top"),sQuery(id+"F5.wireOp",EDGE,"E0.left"),sQuery(id+"F5.wireOp",EDGE,"E0.right")])]}),"instanceName":"1"}),"instanceName":"1"}),"instanceName":"1"});
            var Q6;
            Q6=makeQuery(id+"F37.opPattern","COPY",BODY,{"derivedFrom":makeQuery(id+"F6.opExtrude","SWEPT_BODY",BODY,{"disambiguationData":[OSD([sQuery(id+"F5.wireOp",EDGE,"E0.bottom"),sQuery(id+"F5.wireOp",EDGE,"E0.top"),sQuery(id+"F5.wireOp",EDGE,"E0.left"),sQuery(id+"F5.wireOp",EDGE,"E0.right")])]}),"instanceName":"1"});
            var Q7;
            Q7=makeQuery(id+"F6.opExtrude","SWEPT_BODY",BODY,{"disambiguationData":[OSD([sQuery(id+"F5.wireOp",EDGE,"E0.bottom"),sQuery(id+"F5.wireOp",EDGE,"E0.top"),sQuery(id+"F5.wireOp",EDGE,"E0.left"),sQuery(id+"F5.wireOp",EDGE,"E0.right")])]});
            var Q8;
            Q8=makeQuery(id+"F30.opPattern","COPY",BODY,{"derivedFrom":makeQuery(id+"F29.opPattern","COPY",BODY,{"derivedFrom":makeQuery(id+"F6.opExtrude","SWEPT_BODY",BODY,{"disambiguationData":[OSD([sQuery(id+"F5.wireOp",EDGE,"E0.bottom"),sQuery(id+"F5.wireOp",EDGE,"E0.top"),sQuery(id+"F5.wireOp",EDGE,"E0.left"),sQuery(id+"F5.wireOp",EDGE,"E0.right")])]}),"instanceName":"1"}),"instanceName":"1"});
            var Q9;
            Q9=makeQuery(id+"F35.opPattern","COPY",FACE,{"derivedFrom":makeQuery(id+"F30.opPattern","COPY",FACE,{"derivedFrom":makeQuery(id+"F29.opPattern","COPY",FACE,{"derivedFrom":makeQuery(id+"F24.opExtrude","SWEPT_FACE",FACE,{"disambiguationData":[OSD([sQuery(id+"F23.wireOp",EDGE,"E51"),sQuery(id+"F23.wireOp",EDGE,"E52")])]}),"instanceName":"1"}),"instanceName":"1"}),"instanceName":"1"});
            mirror(context, id + "F38", {"operationType" : NewBodyOperationType.ADD, "entities" : qUnion([Q0, Q1, Q2, Q3, Q4, Q5, Q6, Q7, Q8]), "mirrorPlane" : qUnion([Q9])});
        }
    });
